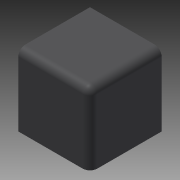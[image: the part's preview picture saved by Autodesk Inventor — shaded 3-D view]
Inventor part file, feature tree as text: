
AUTODESK INVENTOR PART (.ipt)
format: ipt  version: 2013 SP2 (Build 170200200, 200)  size: 105,472 bytes
history: native  units: mm
features: extrude x1, fillet x1, sketch x1, reference x1
ambient origin geometry x8: Origin, YZ Plane, XZ Plane, XY Plane, X Axis, Y Axis, Z Axis, Center Point
bodies: Solid1 (feature_tree)
feature tree (4):
  extrude  "Extrusion1"  Depth=2.0mm
  fillet  "Fillet1"  [1 undecoded]
  sketch  "Sketch1"  dims[d0=20.0mm d1=0.0mm d2=2.0mm]
  reference  "Reference1"
note: 1 required parameter value undecoded (feature->parameter linkage not recoverable at this tier; creation-order binding heuristic only, values carry confidence <= 0.55)
